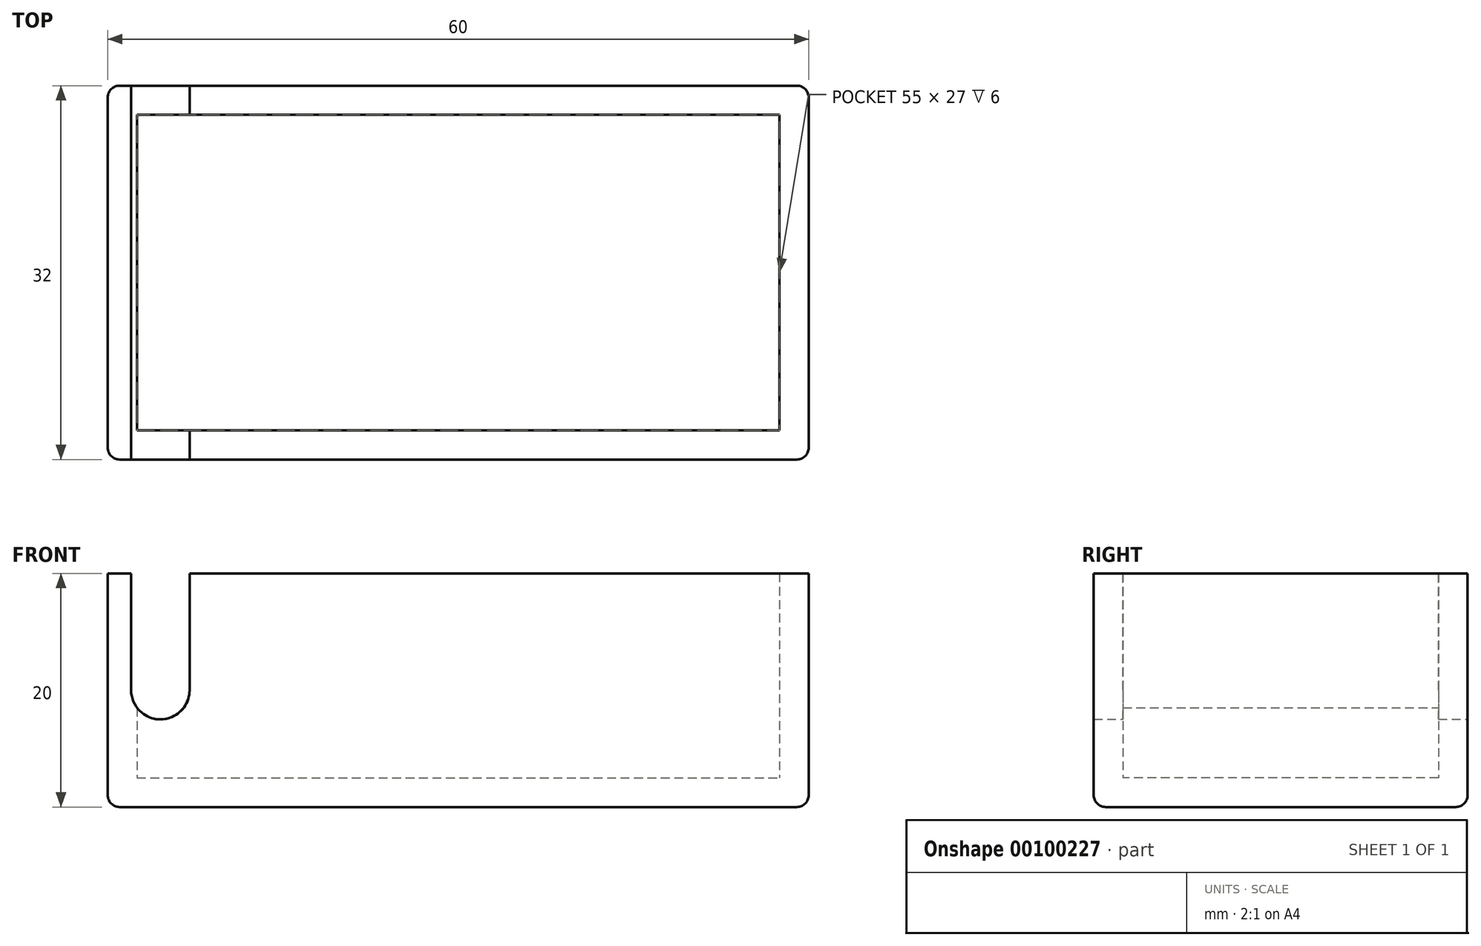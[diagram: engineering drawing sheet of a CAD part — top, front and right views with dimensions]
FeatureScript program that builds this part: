
annotation { "Feature Type Name" : "Feature", "Feature Type Description" : "" }
export const myFeature = defineFeature(function(context is Context, id is Id, definition is map)
    precondition{}
    {
        {
            var Q0;
            Q0=qCreatedBy(makeId("Top.planeOp"),FACE);
            var sketch = newSketch(context, id + "F0", { "sketchPlane" : qUnion([Q0])});
            skLineSegment(sketch, "E0.bottom", {"start": v(-30, 16) * mm, "end": v(30, 16) * mm});
            skLineSegment(sketch, "E0.top", {"start": v(-30, -16) * mm, "end": v(30, -16) * mm});
            skLineSegment(sketch, "E0.left", {"start": v(-30, 16) * mm, "end": v(-30, -16) * mm});
            skLineSegment(sketch, "E0.right", {"start": v(30, 16) * mm, "end": v(30, -16) * mm});
            skPoint(sketch, "E0.middle", {"position": v(0, 0) * mm});
            skSolve(sketch);
        }
        {
            var Q0;
            Q0=makeQuery(id+"F0.imprint","IMPRINT",FACE,{"disambiguationData":[TD([[makeQuery(id+"F0.imprint","IMPRINT",EDGE,{"derivedFrom":sQuery(id+"F0.wireOp",EDGE,"E0.bottom")}),-1.0]])]});
            extrude(context, id + "F1", {"entities" : qUnion([Q0]), "depth" : 20 * mm});
        }
        {
            var Q0;
            Q0=makeQuery(id+"F1.opExtrude","CAP_FACE",FACE,{"disambiguationData":[OSD([sQuery(id+"F0.wireOp",EDGE,"E0.bottom"),sQuery(id+"F0.wireOp",EDGE,"E0.top"),sQuery(id+"F0.wireOp",EDGE,"E0.left"),sQuery(id+"F0.wireOp",EDGE,"E0.right")])],"isStart":false});
            shell(context, id + "F2", {"entities" : qUnion([Q0]), "thickness" : 2.5 * mm});
        }
        {
            var Q0;
            Q0=makeQuery(id+"F1.opExtrude","SWEPT_FACE",FACE,{"disambiguationData":[OSD([sQuery(id+"F0.wireOp",EDGE,"E0.bottom")])]});
            var sketch = newSketch(context, id + "F3", { "sketchPlane" : qUnion([Q0])});
            skLineSegment(sketch, "E1", {"start": v(23, 10) * mm, "end": v(23, 20) * mm});
            skLineSegment(sketch, "E2", {"start": v(28, 20) * mm, "end": v(28, 10) * mm});
            skArc(sketch, "E3", {"start": v(28, 10) * mm, "mid": v(25.5, 7.5) * mm, "end": v(23, 10) * mm});
            skLineSegment(sketch, "E4", {"start": v(28, 20) * mm, "end": v(23, 20) * mm});
            skSolve(sketch);
        }
        {
            var Q0;
            Q0=makeQuery(id+"F3.imprint","IMPRINT",FACE,{"disambiguationData":[TD([[makeQuery(id+"F3.imprint","IMPRINT",EDGE,{"derivedFrom":sQuery(id+"F3.wireOp",EDGE,"E1")}),-1.0]])]});
            extrude(context, id + "F4", {"entities" : qUnion([Q0]), "operationType" : NewBodyOperationType.REMOVE, "endBound" : BoundingType.THROUGH_ALL, "oppositeDirection" : true, "depth" : 25 * mm});
        }
        {
            var Q0;
            Q0=makeQuery(id+"F1.opExtrude","SWEPT_EDGE",EDGE,{"disambiguationData":[OSD([sQuery(id+"F0.wireOp",EDGE,"E0.top"),sQuery(id+"F0.wireOp",EDGE,"E0.right")])]});
            var Q1;
            Q1=makeQuery(id+"F1.opExtrude","CAP_EDGE",EDGE,{"disambiguationData":[OSD([sQuery(id+"F0.wireOp",EDGE,"E0.top")])],"isStart":true});
            var Q2;
            Q2=makeQuery(id+"F1.opExtrude","SWEPT_EDGE",EDGE,{"disambiguationData":[OSD([sQuery(id+"F0.wireOp",EDGE,"E0.bottom"),sQuery(id+"F0.wireOp",EDGE,"E0.right")])]});
            var Q3;
            Q3=makeQuery(id+"F1.opExtrude","CAP_EDGE",EDGE,{"disambiguationData":[OSD([sQuery(id+"F0.wireOp",EDGE,"E0.right")])],"isStart":true});
            var Q4;
            Q4=makeQuery(id+"F1.opExtrude","SWEPT_EDGE",EDGE,{"disambiguationData":[OSD([sQuery(id+"F0.wireOp",EDGE,"E0.top"),sQuery(id+"F0.wireOp",EDGE,"E0.left")])]});
            var Q5;
            Q5=makeQuery(id+"F1.opExtrude","SWEPT_EDGE",EDGE,{"disambiguationData":[OSD([sQuery(id+"F0.wireOp",EDGE,"E0.bottom"),sQuery(id+"F0.wireOp",EDGE,"E0.left")])]});
            var Q6;
            Q6=makeQuery(id+"F1.opExtrude","CAP_EDGE",EDGE,{"disambiguationData":[OSD([sQuery(id+"F0.wireOp",EDGE,"E0.left")])],"isStart":true});
            var Q7;
            Q7=makeQuery(id+"F1.opExtrude","CAP_EDGE",EDGE,{"disambiguationData":[OSD([sQuery(id+"F0.wireOp",EDGE,"E0.bottom")])],"isStart":true});
            fillet(context, id + "F5", {"entities" : qUnion([Q0, Q1, Q2, Q3, Q4, Q5, Q6, Q7]), "radius" : 1 * mm, "tangentPropagation" : true, "allowEdgeOverflow" : false});
        }
    });
